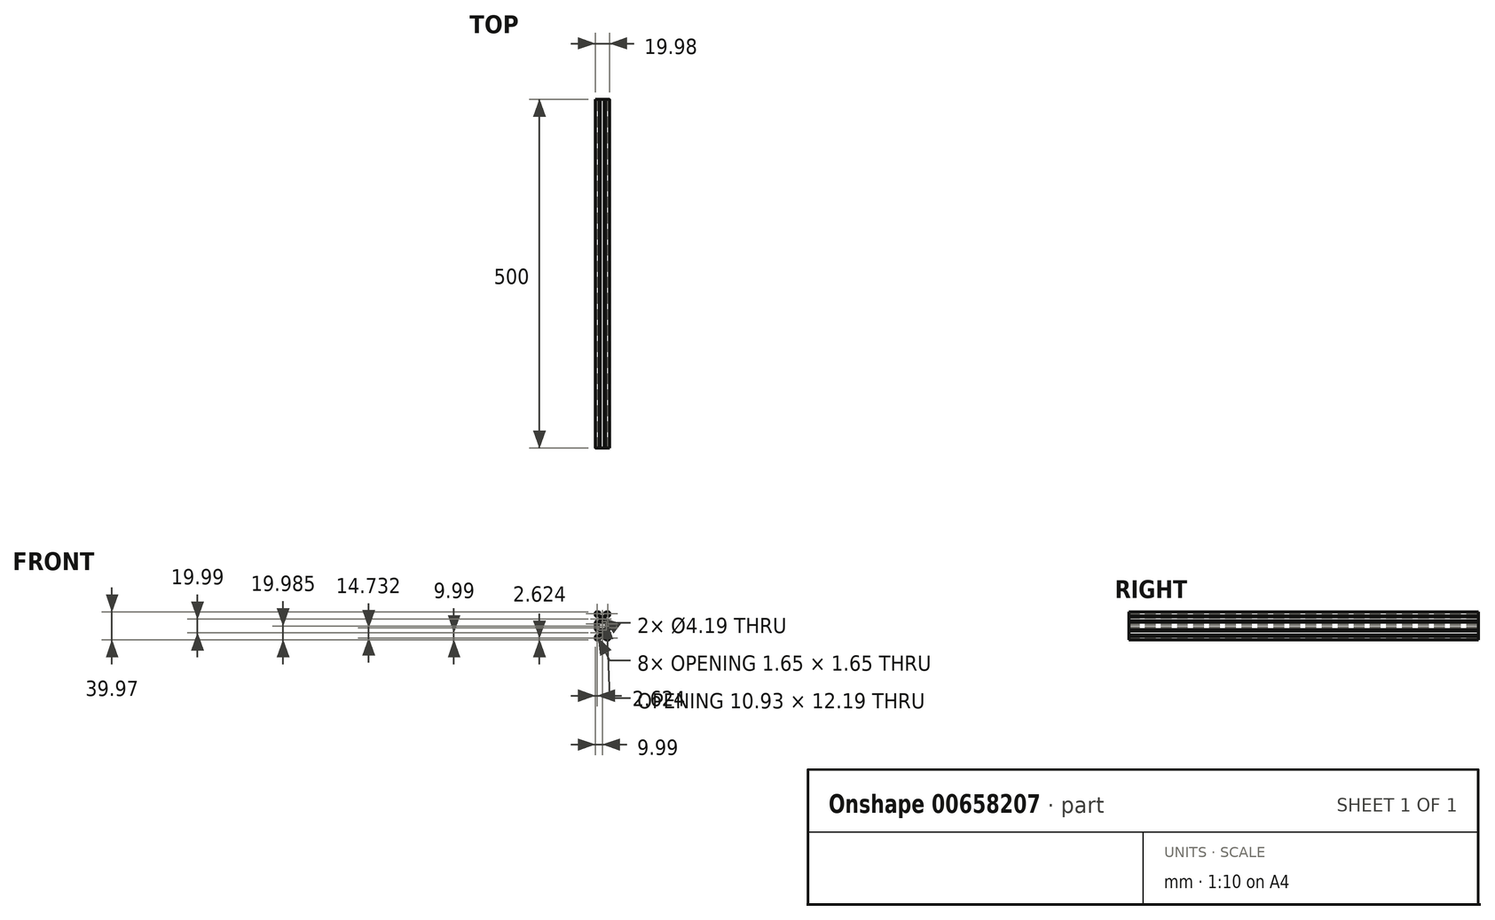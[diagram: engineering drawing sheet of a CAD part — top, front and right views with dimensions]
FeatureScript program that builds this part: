
annotation { "Feature Type Name" : "Feature", "Feature Type Description" : "" }
export const myFeature = defineFeature(function(context is Context, id is Id, definition is map)
    precondition{}
    {
        {
            var Q0;
            Q0=qCreatedBy(makeId("Front.planeOp"),FACE);
            var sketch = newSketch(context, id + "F0", { "sketchPlane" : qUnion([Q0])});
            skLineSegment(sketch, "E0.top", {"start": v(-9, -10) * mm, "end": v(-4.62, -10) * mm});
            skLineSegment(sketch, "E0.left", {"start": v(-10, 9) * mm, "end": v(-10, 4.62) * mm});
            skLineSegment(sketch, "E0.right", {"start": v(10, 9) * mm, "end": v(10, 4.62) * mm});
            skPoint(sketch, "E0.middle", {"position": v(0, 0) * mm});
            skPoint(sketch, "E1.visualSharp", {"position": v(10, 10) * mm});
            skPoint(sketch, "E2.visualSharp", {"position": v(10, -10) * mm});
            skArc(sketch, "E2.filletArc", {"start": v(9, -10) * mm, "mid": v(9.7, -9.7) * mm, "end": v(10, -9) * mm});
            skPoint(sketch, "E3.visualSharp", {"position": v(-10, -10) * mm});
            skArc(sketch, "E3.filletArc", {"start": v(-10, -9) * mm, "mid": v(-9.7, -9.7) * mm, "end": v(-9, -10) * mm});
            skPoint(sketch, "E4.visualSharp", {"position": v(-10, 10) * mm});
            skCircle(sketch, "E5", {"center": v(0, 0) * mm, "radius": 2.1 * mm});
            skLineSegment(sketch, "E6.bottom", {"start": v(2.82, -3.9) * mm, "end": v(-2.82, -3.9) * mm});
            skLineSegment(sketch, "E6.top", {"start": v(2.82, 3.9) * mm, "end": v(-2.82, 3.9) * mm});
            skLineSegment(sketch, "E6.left", {"start": v(3.9, -2.82) * mm, "end": v(3.9, 2.82) * mm});
            skLineSegment(sketch, "E6.right", {"start": v(-3.9, -2.82) * mm, "end": v(-3.9, 2.82) * mm});
            skLineSegment(sketch, "E7.0", {"start": v(-6.54, 5.46) * mm, "end": v(-3.9, 2.82) * mm});
            skLineSegment(sketch, "E8.0", {"start": v(-5.46, 6.54) * mm, "end": v(-2.82, 3.9) * mm});
            skLineSegment(sketch, "E9.0", {"start": v(5.46, 6.54) * mm, "end": v(2.82, 3.9) * mm});
            skLineSegment(sketch, "E10.0", {"start": v(6.54, 5.46) * mm, "end": v(3.9, 2.82) * mm});
            skPoint(sketch, "E11.orphan", {"position": v(3.9, 3.9) * mm});
            skPoint(sketch, "E12.orphan", {"position": v(-3.9, 3.9) * mm});
            skPoint(sketch, "E13.orphan", {"position": v(-3.9, -3.9) * mm});
            skPoint(sketch, "E14.orphan", {"position": v(3.9, -3.9) * mm});
            skLineSegment(sketch, "E15.trimOffspring", {"start": v(3.9, -2.82) * mm, "end": v(6.54, -5.46) * mm});
            skLineSegment(sketch, "E16.trimOffspring", {"start": v(2.82, -3.9) * mm, "end": v(5.46, -6.54) * mm});
            skLineSegment(sketch, "E17.trimOffspring", {"start": v(-2.82, -3.9) * mm, "end": v(-5.46, -6.54) * mm});
            skLineSegment(sketch, "E18.trimOffspring", {"start": v(-3.9, -2.82) * mm, "end": v(-6.54, -5.46) * mm});
            skLineSegment(sketch, "E19.MirrorCS", {"start": v(10, 4.62) * mm, "end": v(8.2, 2.82) * mm});
            skLineSegment(sketch, "E20.MirrorCS", {"start": v(8.2, 2.82) * mm, "end": v(8.2, 5.46) * mm});
            skLineSegment(sketch, "E21.MirrorCS", {"start": v(8.2, 5.46) * mm, "end": v(6.54, 5.46) * mm});
            skLineSegment(sketch, "E22.MirrorCS", {"start": v(-10, 4.62) * mm, "end": v(-8.2, 2.82) * mm});
            skLineSegment(sketch, "E23.MirrorCS", {"start": v(-8.2, 2.82) * mm, "end": v(-8.2, 5.46) * mm});
            skLineSegment(sketch, "E24.MirrorCS", {"start": v(-8.2, 5.46) * mm, "end": v(-6.54, 5.46) * mm});
            skLineSegment(sketch, "E25.MirrorCS", {"start": v(8.2, -5.46) * mm, "end": v(6.54, -5.46) * mm});
            skLineSegment(sketch, "E26.MirrorCS", {"start": v(8.2, -2.82) * mm, "end": v(8.2, -5.46) * mm});
            skLineSegment(sketch, "E27.MirrorCS", {"start": v(10, -4.62) * mm, "end": v(8.2, -2.82) * mm});
            skLineSegment(sketch, "E28.MirrorCS", {"start": v(-10, -4.62) * mm, "end": v(-8.2, -2.82) * mm});
            skLineSegment(sketch, "E29.MirrorCS", {"start": v(-8.2, -2.82) * mm, "end": v(-8.2, -5.46) * mm});
            skLineSegment(sketch, "E30.MirrorCS", {"start": v(-8.2, -5.46) * mm, "end": v(-6.54, -5.46) * mm});
            skLineSegment(sketch, "E31.MirrorCS", {"start": v(-5.46, -8.2) * mm, "end": v(-5.46, -6.54) * mm});
            skLineSegment(sketch, "E32.MirrorCS", {"start": v(-2.82, -8.2) * mm, "end": v(-5.46, -8.2) * mm});
            skLineSegment(sketch, "E33.MirrorCS", {"start": v(-4.62, -10) * mm, "end": v(-2.82, -8.2) * mm});
            skLineSegment(sketch, "E34.MirrorCS", {"start": v(4.62, -10) * mm, "end": v(2.82, -8.2) * mm});
            skLineSegment(sketch, "E35.MirrorCS", {"start": v(2.82, -8.2) * mm, "end": v(5.46, -8.2) * mm});
            skLineSegment(sketch, "E36.MirrorCS", {"start": v(5.46, -8.2) * mm, "end": v(5.46, -6.54) * mm});
            skLineSegment(sketch, "E37", {"start": v(-8.2, -8.04) * mm, "end": v(-8.2, -6.7) * mm});
            skLineSegment(sketch, "E38", {"start": v(-8.04, -8.2) * mm, "end": v(-6.7, -8.2) * mm});
            skLineSegment(sketch, "E39", {"start": v(-6.54, -8.04) * mm, "end": v(-6.54, -7.99) * mm});
            skLineSegment(sketch, "E40", {"start": v(-8.04, -6.54) * mm, "end": v(-7.99, -6.54) * mm});
            skLineSegment(sketch, "E41", {"start": v(-7.99, -6.54) * mm, "end": v(-6.54, -7.99) * mm});
            skPoint(sketch, "E42.visualSharp", {"position": v(-8.2, -8.2) * mm});
            skArc(sketch, "E42.filletArc", {"start": v(-8.2, -8.04) * mm, "mid": v(-8.15, -8.15) * mm, "end": v(-8.04, -8.2) * mm});
            skPoint(sketch, "E43.visualSharp", {"position": v(-6.54, -8.2) * mm});
            skArc(sketch, "E43.filletArc", {"start": v(-6.7, -8.2) * mm, "mid": v(-6.59, -8.15) * mm, "end": v(-6.54, -8.04) * mm});
            skPoint(sketch, "E44.visualSharp", {"position": v(-8.2, -6.54) * mm});
            skArc(sketch, "E44.filletArc", {"start": v(-8.04, -6.54) * mm, "mid": v(-8.15, -6.59) * mm, "end": v(-8.2, -6.7) * mm});
            skLineSegment(sketch, "E45.MirrorCS", {"start": v(8.2, -8.04) * mm, "end": v(8.2, -6.7) * mm});
            skArc(sketch, "E46.MirrorCS", {"start": v(8.2, -8.04) * mm, "mid": v(8.15, -8.15) * mm, "end": v(8.04, -8.2) * mm});
            skLineSegment(sketch, "E47.MirrorCS", {"start": v(8.04, -8.2) * mm, "end": v(6.7, -8.2) * mm});
            skArc(sketch, "E48.MirrorCS", {"start": v(6.7, -8.2) * mm, "mid": v(6.59, -8.15) * mm, "end": v(6.54, -8.04) * mm});
            skLineSegment(sketch, "E49.MirrorCS", {"start": v(6.54, -8.04) * mm, "end": v(6.54, -7.99) * mm});
            skLineSegment(sketch, "E50.MirrorCS", {"start": v(7.99, -6.54) * mm, "end": v(6.54, -7.99) * mm});
            skArc(sketch, "E51.MirrorCS", {"start": v(8.04, -6.54) * mm, "mid": v(8.15, -6.59) * mm, "end": v(8.2, -6.7) * mm});
            skLineSegment(sketch, "E52.MirrorCS", {"start": v(8.04, -6.54) * mm, "end": v(7.99, -6.54) * mm});
            skLineSegment(sketch, "E53.MirrorCS", {"start": v(8.04, 6.54) * mm, "end": v(7.99, 6.54) * mm});
            skLineSegment(sketch, "E54.MirrorCS", {"start": v(6.54, 8.04) * mm, "end": v(6.54, 7.99) * mm});
            skArc(sketch, "E55.MirrorCS", {"start": v(8.04, 6.54) * mm, "mid": v(8.15, 6.59) * mm, "end": v(8.2, 6.7) * mm});
            skArc(sketch, "E56.MirrorCS", {"start": v(6.7, 8.2) * mm, "mid": v(6.59, 8.15) * mm, "end": v(6.54, 8.04) * mm});
            skArc(sketch, "E57.MirrorCS", {"start": v(8.2, 8.04) * mm, "mid": v(8.15, 8.15) * mm, "end": v(8.04, 8.2) * mm});
            skLineSegment(sketch, "E58.MirrorCS", {"start": v(8.2, 8.04) * mm, "end": v(8.2, 6.7) * mm});
            skLineSegment(sketch, "E59.MirrorCS", {"start": v(8.04, 8.2) * mm, "end": v(6.7, 8.2) * mm});
            skLineSegment(sketch, "E60.MirrorCS", {"start": v(7.99, 6.54) * mm, "end": v(6.54, 7.99) * mm});
            skArc(sketch, "E61.MirrorCS", {"start": v(-8.04, 6.54) * mm, "mid": v(-8.15, 6.59) * mm, "end": v(-8.2, 6.7) * mm});
            skArc(sketch, "E62.MirrorCS", {"start": v(-6.7, 8.2) * mm, "mid": v(-6.59, 8.15) * mm, "end": v(-6.54, 8.04) * mm});
            skArc(sketch, "E63.MirrorCS", {"start": v(-8.2, 8.04) * mm, "mid": v(-8.15, 8.15) * mm, "end": v(-8.04, 8.2) * mm});
            skLineSegment(sketch, "E64.MirrorCS", {"start": v(-8.04, 6.54) * mm, "end": v(-7.99, 6.54) * mm});
            skLineSegment(sketch, "E65.MirrorCS", {"start": v(-6.54, 8.04) * mm, "end": v(-6.54, 7.99) * mm});
            skPoint(sketch, "E66.MirrorP", {"position": v(-8.2, 6.54) * mm});
            skPoint(sketch, "E67.MirrorP", {"position": v(-8.2, 8.2) * mm});
            skLineSegment(sketch, "E68.MirrorCS", {"start": v(-8.2, 8.04) * mm, "end": v(-8.2, 6.7) * mm});
            skLineSegment(sketch, "E69.MirrorCS", {"start": v(-7.99, 6.54) * mm, "end": v(-6.54, 7.99) * mm});
            skLineSegment(sketch, "E70.MirrorCS", {"start": v(-8.04, 8.2) * mm, "end": v(-6.7, 8.2) * mm});
            skPoint(sketch, "E71.MirrorP", {"position": v(-6.54, 8.2) * mm});
            skLineSegment(sketch, "E72.trimOffspring", {"start": v(10, -4.62) * mm, "end": v(10, -9) * mm});
            skLineSegment(sketch, "E73.trimOffspring", {"start": v(-10, -4.62) * mm, "end": v(-10, -9) * mm});
            skLineSegment(sketch, "E74.trimOffspring", {"start": v(4.62, -10) * mm, "end": v(9, -10) * mm});
            skArc(sketch, "E75.MirrorCS", {"start": v(-8.04, 13.45) * mm, "mid": v(-8.15, 13.4) * mm, "end": v(-8.2, 13.3) * mm});
            skLineSegment(sketch, "E76.MirrorCS", {"start": v(-8.04, 13.45) * mm, "end": v(-7.99, 13.45) * mm});
            skArc(sketch, "E77.MirrorCS", {"start": v(-8.2, 11.95) * mm, "mid": v(-8.15, 11.84) * mm, "end": v(-8.04, 11.8) * mm});
            skLineSegment(sketch, "E78.MirrorCS", {"start": v(-8.2, 11.95) * mm, "end": v(-8.2, 13.3) * mm});
            skLineSegment(sketch, "E79.MirrorCS", {"start": v(-6.54, 11.95) * mm, "end": v(-6.54, 12) * mm});
            skArc(sketch, "E80.MirrorCS", {"start": v(6.7, 11.8) * mm, "mid": v(6.59, 11.84) * mm, "end": v(6.54, 11.95) * mm});
            skArc(sketch, "E81.MirrorCS", {"start": v(-6.7, 11.8) * mm, "mid": v(-6.59, 11.84) * mm, "end": v(-6.54, 11.95) * mm});
            skLineSegment(sketch, "E82.MirrorCS", {"start": v(6.54, 11.95) * mm, "end": v(6.54, 12) * mm});
            skLineSegment(sketch, "E83.MirrorCS", {"start": v(-7.99, 13.45) * mm, "end": v(-6.54, 12) * mm});
            skLineSegment(sketch, "E84.MirrorCS", {"start": v(-8.04, 11.8) * mm, "end": v(-6.7, 11.8) * mm});
            skLineSegment(sketch, "E85.MirrorCS", {"start": v(8.04, 11.8) * mm, "end": v(6.7, 11.8) * mm});
            skLineSegment(sketch, "E86.MirrorCS", {"start": v(7.99, 13.45) * mm, "end": v(6.54, 12) * mm});
            skLineSegment(sketch, "E87.MirrorCS", {"start": v(8.04, 13.45) * mm, "end": v(7.99, 13.45) * mm});
            skArc(sketch, "E88.MirrorCS", {"start": v(8.2, 11.95) * mm, "mid": v(8.15, 11.84) * mm, "end": v(8.04, 11.8) * mm});
            skLineSegment(sketch, "E89.MirrorCS", {"start": v(8.2, 11.95) * mm, "end": v(8.2, 13.3) * mm});
            skLineSegment(sketch, "E90.MirrorCS", {"start": v(-6.54, 28.03) * mm, "end": v(-6.54, 27.98) * mm});
            skArc(sketch, "E91.MirrorCS", {"start": v(8.04, 13.45) * mm, "mid": v(8.15, 13.4) * mm, "end": v(8.2, 13.3) * mm});
            skArc(sketch, "E92.MirrorCS", {"start": v(-6.7, 28.18) * mm, "mid": v(-6.59, 28.14) * mm, "end": v(-6.54, 28.03) * mm});
            skArc(sketch, "E93.MirrorCS", {"start": v(-8.04, 26.53) * mm, "mid": v(-8.15, 26.57) * mm, "end": v(-8.2, 26.68) * mm});
            skLineSegment(sketch, "E94.MirrorCS", {"start": v(-7.99, 26.53) * mm, "end": v(-6.54, 27.98) * mm});
            skLineSegment(sketch, "E95.MirrorCS", {"start": v(-8.04, 28.18) * mm, "end": v(-6.7, 28.18) * mm});
            skLineSegment(sketch, "E96.MirrorCS", {"start": v(-8.04, 26.53) * mm, "end": v(-7.99, 26.53) * mm});
            skLineSegment(sketch, "E97.MirrorCS", {"start": v(-8.2, 28.03) * mm, "end": v(-8.2, 26.68) * mm});
            skArc(sketch, "E98.MirrorCS", {"start": v(6.7, 28.18) * mm, "mid": v(6.59, 28.14) * mm, "end": v(6.54, 28.03) * mm});
            skLineSegment(sketch, "E99.MirrorCS", {"start": v(6.54, 28.03) * mm, "end": v(6.54, 27.98) * mm});
            skArc(sketch, "E100.MirrorCS", {"start": v(-8.2, 28.03) * mm, "mid": v(-8.15, 28.14) * mm, "end": v(-8.04, 28.18) * mm});
            skArc(sketch, "E101.MirrorCS", {"start": v(8.2, 28.03) * mm, "mid": v(8.15, 28.14) * mm, "end": v(8.04, 28.18) * mm});
            skLineSegment(sketch, "E102.MirrorCS", {"start": v(8.04, 28.18) * mm, "end": v(6.7, 28.18) * mm});
            skLineSegment(sketch, "E103.MirrorCS", {"start": v(7.99, 26.53) * mm, "end": v(6.54, 27.98) * mm});
            skArc(sketch, "E104.MirrorCS", {"start": v(8.04, 26.53) * mm, "mid": v(8.15, 26.57) * mm, "end": v(8.2, 26.68) * mm});
            skLineSegment(sketch, "E105.MirrorCS", {"start": v(8.2, 28.03) * mm, "end": v(8.2, 26.68) * mm});
            skLineSegment(sketch, "E106.MirrorCS", {"start": v(8.2, 14.53) * mm, "end": v(6.54, 14.53) * mm});
            skLineSegment(sketch, "E107.MirrorCS", {"start": v(8.04, 26.53) * mm, "end": v(7.99, 26.53) * mm});
            skArc(sketch, "E108.MirrorCS", {"start": v(-10, 29) * mm, "mid": v(-9.7, 29.7) * mm, "end": v(-9, 29.98) * mm});
            skLineSegment(sketch, "E109.MirrorCS", {"start": v(-8.2, 25.45) * mm, "end": v(-6.54, 25.45) * mm});
            skLineSegment(sketch, "E110.MirrorCS", {"start": v(-5.46, 28.18) * mm, "end": v(-5.46, 26.53) * mm});
            skLineSegment(sketch, "E111.MirrorCS", {"start": v(5.46, 28.18) * mm, "end": v(5.46, 26.53) * mm});
            skLineSegment(sketch, "E112.MirrorCS", {"start": v(5.46, 13.45) * mm, "end": v(2.82, 16.1) * mm});
            skArc(sketch, "E113.MirrorCS", {"start": v(9, 29.98) * mm, "mid": v(9.7, 29.7) * mm, "end": v(10, 29) * mm});
            skLineSegment(sketch, "E114.MirrorCS", {"start": v(8.2, 17.17) * mm, "end": v(8.2, 14.53) * mm});
            skLineSegment(sketch, "E115.MirrorCS", {"start": v(8.2, 25.45) * mm, "end": v(6.54, 25.45) * mm});
            skLineSegment(sketch, "E116.MirrorCS", {"start": v(-10, 10.99) * mm, "end": v(-10, 15.37) * mm});
            skLineSegment(sketch, "E117.MirrorCS", {"start": v(-8.2, 14.53) * mm, "end": v(-6.54, 14.53) * mm});
            skLineSegment(sketch, "E118.MirrorCS", {"start": v(-2.82, 23.89) * mm, "end": v(-5.46, 26.53) * mm});
            skLineSegment(sketch, "E119.MirrorCS", {"start": v(10, 24.61) * mm, "end": v(8.2, 22.81) * mm});
            skLineSegment(sketch, "E120.MirrorCS", {"start": v(2.82, 23.89) * mm, "end": v(5.46, 26.53) * mm});
            skLineSegment(sketch, "E121.MirrorCS", {"start": v(8.2, 22.81) * mm, "end": v(8.2, 25.45) * mm});
            skLineSegment(sketch, "E122.MirrorCS", {"start": v(-3.9, 22.81) * mm, "end": v(-6.54, 25.45) * mm});
            skLineSegment(sketch, "E123.MirrorCS", {"start": v(-10, 24.61) * mm, "end": v(-8.2, 22.81) * mm});
            skLineSegment(sketch, "E124.MirrorCS", {"start": v(-8.2, 22.81) * mm, "end": v(-8.2, 25.45) * mm});
            skPoint(sketch, "E125.MirrorP", {"position": v(-8.2, 13.45) * mm});
            skLineSegment(sketch, "E126.MirrorCS", {"start": v(-2.82, 28.18) * mm, "end": v(-5.46, 28.18) * mm});
            skLineSegment(sketch, "E127.MirrorCS", {"start": v(3.9, 22.81) * mm, "end": v(6.54, 25.45) * mm});
            skLineSegment(sketch, "E128.MirrorCS", {"start": v(-4.62, 29.98) * mm, "end": v(-2.82, 28.18) * mm});
            skLineSegment(sketch, "E129.MirrorCS", {"start": v(2.82, 28.18) * mm, "end": v(5.46, 28.18) * mm});
            skLineSegment(sketch, "E130.MirrorCS", {"start": v(-8.2, 17.17) * mm, "end": v(-8.2, 14.53) * mm});
            skLineSegment(sketch, "E131.MirrorCS", {"start": v(-5.46, 13.45) * mm, "end": v(-2.82, 16.1) * mm});
            skPoint(sketch, "E132.MirrorP", {"position": v(0, 19.99) * mm});
            skLineSegment(sketch, "E133.MirrorCS", {"start": v(4.62, 29.98) * mm, "end": v(2.82, 28.18) * mm});
            skLineSegment(sketch, "E134.MirrorCS", {"start": v(-6.54, 14.53) * mm, "end": v(-3.9, 17.17) * mm});
            skLineSegment(sketch, "E135.MirrorCS", {"start": v(-9, 29.98) * mm, "end": v(-4.62, 29.98) * mm});
            skLineSegment(sketch, "E136.MirrorCS", {"start": v(-10, 24.61) * mm, "end": v(-10, 29) * mm});
            skLineSegment(sketch, "E137.MirrorCS", {"start": v(10, 15.37) * mm, "end": v(8.2, 17.17) * mm});
            skLineSegment(sketch, "E138.MirrorCS", {"start": v(-10, 15.37) * mm, "end": v(-8.2, 17.17) * mm});
            skLineSegment(sketch, "E139.MirrorCS", {"start": v(6.54, 14.53) * mm, "end": v(3.9, 17.17) * mm});
            skPoint(sketch, "E140.MirrorP", {"position": v(-6.54, 28.18) * mm});
            skPoint(sketch, "E141.MirrorP", {"position": v(-8.2, 26.53) * mm});
            skPoint(sketch, "E142.MirrorP", {"position": v(-8.2, 11.8) * mm});
            skPoint(sketch, "E143.MirrorP", {"position": v(-8.2, 28.18) * mm});
            skPoint(sketch, "E144.MirrorP", {"position": v(-6.54, 11.8) * mm});
            skLineSegment(sketch, "E145.MirrorCS", {"start": v(2.82, 23.89) * mm, "end": v(-2.82, 23.89) * mm});
            skPoint(sketch, "E146.MirrorP", {"position": v(10, 29.98) * mm});
            skPoint(sketch, "E147.MirrorP", {"position": v(-10, 29.98) * mm});
            skPoint(sketch, "E148.MirrorP", {"position": v(3.9, 23.89) * mm});
            skPoint(sketch, "E149.MirrorP", {"position": v(-3.9, 16.1) * mm});
            skLineSegment(sketch, "E150.MirrorCS", {"start": v(10, 24.61) * mm, "end": v(10, 29) * mm});
            skCircle(sketch, "E151.MirrorC", {"center": v(0, 19.99) * mm, "radius": 2.1 * mm});
            skLineSegment(sketch, "E152.MirrorCS", {"start": v(2.82, 16.1) * mm, "end": v(-2.82, 16.1) * mm});
            skLineSegment(sketch, "E153.MirrorCS", {"start": v(4.62, 29.98) * mm, "end": v(9, 29.98) * mm});
            skLineSegment(sketch, "E154.MirrorCS", {"start": v(-3.9, 22.81) * mm, "end": v(-3.9, 17.17) * mm});
            skPoint(sketch, "E155.MirrorP", {"position": v(3.9, 16.1) * mm});
            skLineSegment(sketch, "E156.MirrorCS", {"start": v(10, 10.99) * mm, "end": v(10, 15.37) * mm});
            skLineSegment(sketch, "E157.MirrorCS", {"start": v(3.9, 22.81) * mm, "end": v(3.9, 17.17) * mm});
            skPoint(sketch, "E158.MirrorP", {"position": v(-3.9, 23.89) * mm});
            skLineSegment(sketch, "E159", {"start": v(5.46, 13.45) * mm, "end": v(5.46, 6.54) * mm});
            skLineSegment(sketch, "E160", {"start": v(-5.46, 13.45) * mm, "end": v(-5.46, 6.54) * mm});
            skLineSegment(sketch, "E161", {"start": v(-10, 10.99) * mm, "end": v(-10, 9) * mm});
            skLineSegment(sketch, "E162", {"start": v(10, 10.99) * mm, "end": v(10, 9) * mm});
            skSolve(sketch);
        }
        {
            assignVariable(context, id + "F1", {"name" : "Length", "anyValue" : 500 * mm});
        }
        {
            var Q0;
            Q0=makeQuery(id+"F0.imprint","IMPRINT",FACE,{"disambiguationData":[TD([[makeQuery(id+"F0.imprint","IMPRINT",EDGE,{"derivedFrom":sQuery(id+"F0.wireOp",EDGE,"E0.top")}),1.0]])]});
            extrude(context, id + "F2", {"entities" : qUnion([Q0]), "depth" : (getVariable(context, 'Length')), "offsetDistance" : 25.4 * mm});
        }
    });
